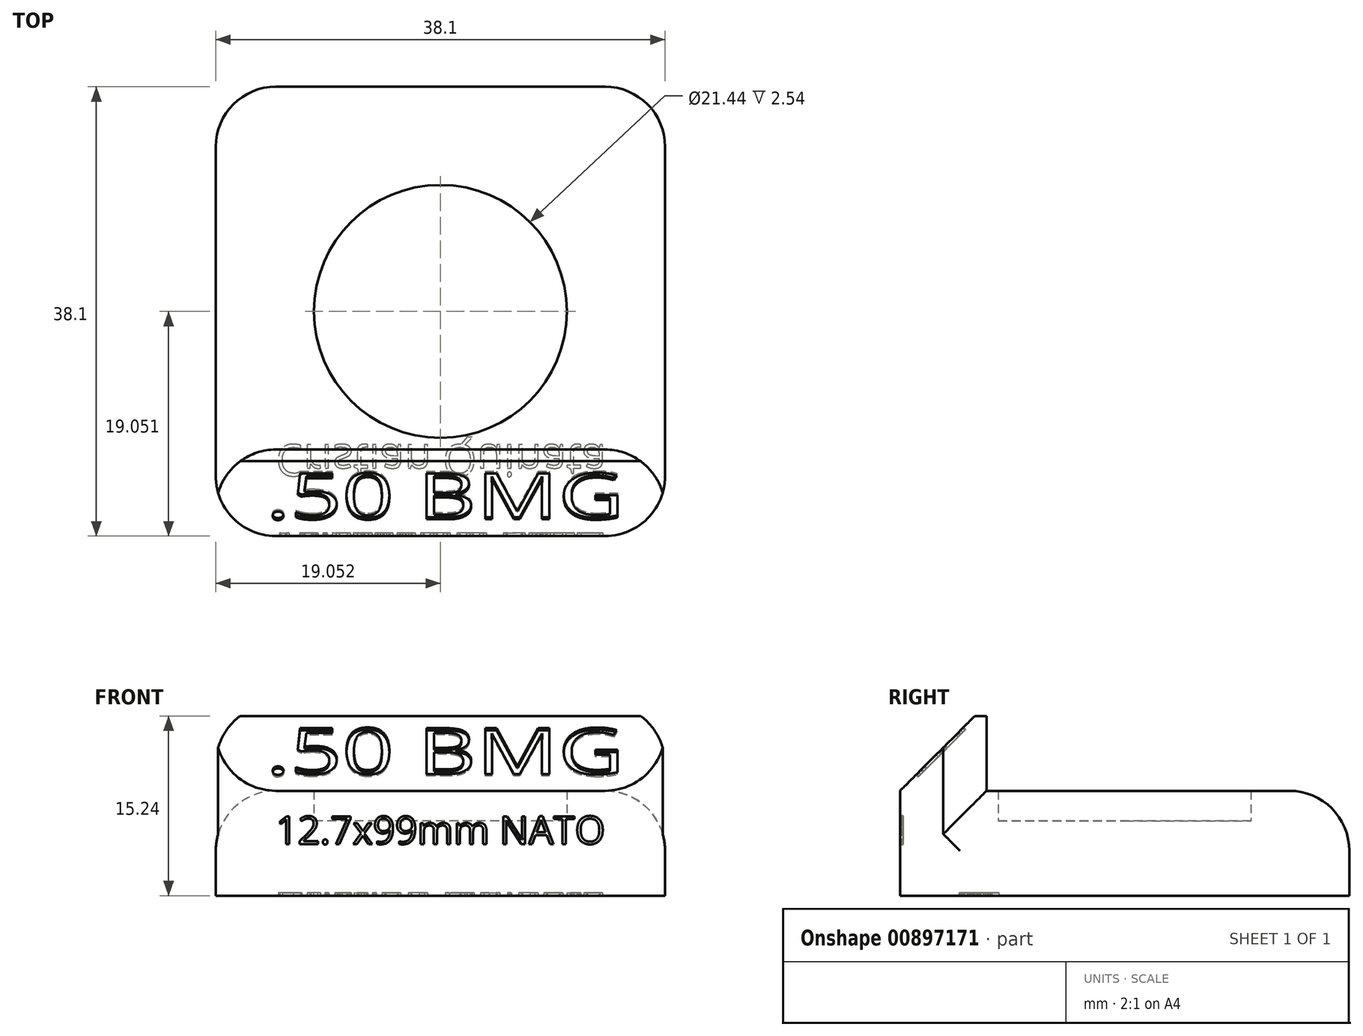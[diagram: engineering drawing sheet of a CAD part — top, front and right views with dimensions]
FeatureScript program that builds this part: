
annotation { "Feature Type Name" : "Feature", "Feature Type Description" : "" }
export const myFeature = defineFeature(function(context is Context, id is Id, definition is map)
    precondition{}
    {
        {
            var Q0;
            Q0=qCreatedBy(makeId("Top.planeOp"),FACE);
            var sketch = newSketch(context, id + "F0", { "sketchPlane" : qUnion([Q0])});
            skLineSegment(sketch, "E0.bottom", {"start": v(-52.13, -21.79) * mm, "end": v(-14.03, -21.79) * mm});
            skLineSegment(sketch, "E0.top", {"start": v(-52.13, -59.89) * mm, "end": v(-14.03, -59.89) * mm});
            skLineSegment(sketch, "E0.left", {"start": v(-52.13, -21.79) * mm, "end": v(-52.13, -59.89) * mm});
            skLineSegment(sketch, "E0.right", {"start": v(-14.03, -21.79) * mm, "end": v(-14.03, -59.89) * mm});
            skLineSegment(sketch, "E1", {"start": v(-33.08, -21.79) * mm, "end": v(-33.08, -59.89) * mm});
            skCircle(sketch, "E2", {"center": v(-33.08, -40.84) * mm, "radius": 10.72 * mm});
            skCircle(sketch, "E3", {"center": v(-33.08, -40.84) * mm, "radius": 10.21 * mm});
            skLineSegment(sketch, "E4", {"start": v(-52.13, -47.19) * mm, "end": v(-39.43, -59.89) * mm});
            skLineSegment(sketch, "E5", {"start": v(-14.03, -47.19) * mm, "end": v(-26.73, -59.89) * mm});
            skLineSegment(sketch, "E6", {"start": v(-52.13, -34.49) * mm, "end": v(-39.43, -21.79) * mm});
            skLineSegment(sketch, "E7", {"start": v(-26.73, -21.79) * mm, "end": v(-14.03, -34.49) * mm});
            skSolve(sketch);
        }
        {
            var Q0;
            {var subQ0=sQuery(id+"F0.wireOp",EDGE,"E2");var subQ1=sQuery(id+"F0.wireOp",EDGE,"E1");var subQ2=makeQuery(id+"F0.imprint","INTERSECT",VERTEX,{"disambiguationData":[OD(0.0)],"derivedFrom":[subQ1,subQ0]});Q0=makeQuery(id+"F0.imprint","IMPRINT",FACE,{"disambiguationData":[TD([[makeQuery(id+"F0.imprint","IMPRINT",EDGE,{"disambiguationData":[TD([[subQ2,-1.0]])],"derivedFrom":subQ1}),-1.0]])]});}
            var Q1;
            {var subQ3=sQuery(id+"F0.wireOp",EDGE,"E4");Q1=makeQuery(id+"F0.imprint","IMPRINT",FACE,{"disambiguationData":[TD([[makeQuery(id+"F0.imprint","IMPRINT",EDGE,{"derivedFrom":subQ3}),-1.0]])]});}
            var Q2;
            {var subQ0=sQuery(id+"F0.wireOp",EDGE,"E3");var subQ1=sQuery(id+"F0.wireOp",EDGE,"E1");var subQ2=makeQuery(id+"F0.imprint","INTERSECT",VERTEX,{"disambiguationData":[OD(0.0)],"derivedFrom":[subQ1,subQ0]});Q2=makeQuery(id+"F0.imprint","IMPRINT",FACE,{"disambiguationData":[TD([[makeQuery(id+"F0.imprint","IMPRINT",EDGE,{"disambiguationData":[TD([[subQ2,-1.0]])],"derivedFrom":subQ1}),-1.0]])]});}
            var Q3;
            {var subQ0=sQuery(id+"F0.wireOp",EDGE,"E3");var subQ1=sQuery(id+"F0.wireOp",EDGE,"E1");var subQ2=makeQuery(id+"F0.imprint","INTERSECT",VERTEX,{"disambiguationData":[OD(0.0)],"derivedFrom":[subQ1,subQ0]});Q3=makeQuery(id+"F0.imprint","IMPRINT",FACE,{"disambiguationData":[TD([[makeQuery(id+"F0.imprint","IMPRINT",EDGE,{"disambiguationData":[TD([[subQ2,-1.0]])],"derivedFrom":subQ1}),1.0]])]});}
            var Q4;
            {var subQ3=sQuery(id+"F0.wireOp",EDGE,"E7");Q4=makeQuery(id+"F0.imprint","IMPRINT",FACE,{"disambiguationData":[TD([[makeQuery(id+"F0.imprint","IMPRINT",EDGE,{"derivedFrom":subQ3}),1.0]])]});}
            var Q5;
            {var subQ3=sQuery(id+"F0.wireOp",EDGE,"E5");Q5=makeQuery(id+"F0.imprint","IMPRINT",FACE,{"disambiguationData":[TD([[makeQuery(id+"F0.imprint","IMPRINT",EDGE,{"derivedFrom":subQ3}),1.0]])]});}
            var Q6;
            {var subQ6=sQuery(id+"F0.wireOp",EDGE,"E4");Q6=makeQuery(id+"F0.imprint","IMPRINT",FACE,{"disambiguationData":[TD([[makeQuery(id+"F0.imprint","IMPRINT",EDGE,{"derivedFrom":subQ6}),1.0]])]});}
            var Q7;
            {var subQ7=sQuery(id+"F0.wireOp",EDGE,"E5");Q7=makeQuery(id+"F0.imprint","IMPRINT",FACE,{"disambiguationData":[TD([[makeQuery(id+"F0.imprint","IMPRINT",EDGE,{"derivedFrom":subQ7}),-1.0]])]});}
            var Q8;
            {var subQ3=sQuery(id+"F0.wireOp",EDGE,"E6");Q8=makeQuery(id+"F0.imprint","IMPRINT",FACE,{"disambiguationData":[TD([[makeQuery(id+"F0.imprint","IMPRINT",EDGE,{"derivedFrom":subQ3}),1.0]])]});}
            var Q9;
            {var subQ0=sQuery(id+"F0.wireOp",EDGE,"E2");var subQ1=sQuery(id+"F0.wireOp",EDGE,"E1");var subQ2=makeQuery(id+"F0.imprint","INTERSECT",VERTEX,{"disambiguationData":[OD(0.0)],"derivedFrom":[subQ1,subQ0]});Q9=makeQuery(id+"F0.imprint","IMPRINT",FACE,{"disambiguationData":[TD([[makeQuery(id+"F0.imprint","IMPRINT",EDGE,{"disambiguationData":[TD([[subQ2,-1.0]])],"derivedFrom":subQ1}),1.0]])]});}
            extrude(context, id + "F1", {"entities" : qUnion([Q0, Q1, Q2, Q3, Q4, Q5, Q6, Q7, Q8, Q9]), "depth" : 6.35 * mm, "offsetDistance" : 25.4 * mm});
        }
        {
            var Q0;
            {var subQ6=sQuery(id+"F0.wireOp",EDGE,"E4");Q0=makeQuery(id+"F0.imprint","IMPRINT",FACE,{"disambiguationData":[TD([[makeQuery(id+"F0.imprint","IMPRINT",EDGE,{"derivedFrom":subQ6}),1.0]])]});}
            var Q1;
            {var subQ7=sQuery(id+"F0.wireOp",EDGE,"E5");Q1=makeQuery(id+"F0.imprint","IMPRINT",FACE,{"disambiguationData":[TD([[makeQuery(id+"F0.imprint","IMPRINT",EDGE,{"derivedFrom":subQ7}),-1.0]])]});}
            var Q2;
            {var subQ3=sQuery(id+"F0.wireOp",EDGE,"E4");Q2=makeQuery(id+"F0.imprint","IMPRINT",FACE,{"disambiguationData":[TD([[makeQuery(id+"F0.imprint","IMPRINT",EDGE,{"derivedFrom":subQ3}),-1.0]])]});}
            var Q3;
            {var subQ3=sQuery(id+"F0.wireOp",EDGE,"E5");Q3=makeQuery(id+"F0.imprint","IMPRINT",FACE,{"disambiguationData":[TD([[makeQuery(id+"F0.imprint","IMPRINT",EDGE,{"derivedFrom":subQ3}),1.0]])]});}
            var Q4;
            {var subQ3=sQuery(id+"F0.wireOp",EDGE,"E7");Q4=makeQuery(id+"F0.imprint","IMPRINT",FACE,{"disambiguationData":[TD([[makeQuery(id+"F0.imprint","IMPRINT",EDGE,{"derivedFrom":subQ3}),1.0]])]});}
            var Q5;
            {var subQ3=sQuery(id+"F0.wireOp",EDGE,"E6");Q5=makeQuery(id+"F0.imprint","IMPRINT",FACE,{"disambiguationData":[TD([[makeQuery(id+"F0.imprint","IMPRINT",EDGE,{"derivedFrom":subQ3}),1.0]])]});}
            extrude(context, id + "F2", {"entities" : qUnion([Q0, Q1, Q2, Q3, Q4, Q5]), "operationType" : NewBodyOperationType.ADD, "depth" : 8.9 * mm, "offsetDistance" : 25.4 * mm});
        }
        {
            var Q0;
            Q0=makeQuery(id+"F2.opExtrude","CAP_FACE",FACE,{"disambiguationData":[OSD([sQuery(id+"F0.wireOp",EDGE,"E0.bottom"),sQuery(id+"F0.wireOp",EDGE,"E0.top"),sQuery(id+"F0.wireOp",EDGE,"E0.left"),sQuery(id+"F0.wireOp",EDGE,"E0.right"),sQuery(id+"F0.wireOp",EDGE,"E2")])],"isStart":false});
            var sketch = newSketch(context, id + "F3", { "sketchPlane" : qUnion([Q0])});
            skLineSegment(sketch, "E8", {"start": v(-52.13, -59.89) * mm, "end": v(-52.13, -52.56) * mm});
            skLineSegment(sketch, "E9", {"start": v(-52.13, -52.56) * mm, "end": v(-14.03, -52.56) * mm});
            skLineSegment(sketch, "E10", {"start": v(-14.03, -52.56) * mm, "end": v(-14.03, -59.89) * mm});
            skLineSegment(sketch, "E11", {"start": v(-14.03, -59.89) * mm, "end": v(-52.13, -59.89) * mm});
            skSolve(sketch);
        }
        {
            var Q0;
            Q0=makeQuery(id+"F3.imprint","IMPRINT",FACE,{"disambiguationData":[TD([[makeQuery(id+"F3.imprint","IMPRINT",EDGE,{"derivedFrom":sQuery(id+"F3.wireOp",EDGE,"E8")}),1.0]])]});
            extrude(context, id + "F4", {"entities" : qUnion([Q0]), "operationType" : NewBodyOperationType.ADD, "depth" : 6.35 * mm, "offsetDistance" : 25.4 * mm});
        }
        {
            var Q0;
            Q0=makeQuery(id+"F4.opExtrude","CAP_EDGE",EDGE,{"disambiguationData":[OSD([sQuery(id+"F3.wireOp",EDGE,"E11")])],"isStart":false});
            chamfer(context, id + "F5", {"entities" : qUnion([Q0]), "width" : 6.35 * mm, "tangentPropagation" : true});
        }
        {
            var Q0;
            {var subQ0=sQuery(id+"F0.wireOp",EDGE,"E0.left");var subQ1=sQuery(id+"F0.wireOp",EDGE,"E0.top");Q0=makeQuery(id+"F4.boolean.opBoolean","MERGE",EDGE,{"derivedFrom":[makeQuery(id+"FzP8uQMfJsJzeae_0.boolean.opBoolean","MERGE",EDGE,{"derivedFrom":[makeQuery(id+"F2.boolean.opBoolean","MERGE",EDGE,{"derivedFrom":[makeQuery(id+"F1.opExtrude","SWEPT_EDGE",EDGE,{"disambiguationData":[OSD([subQ1,subQ0])]}),makeQuery(id+"F2.opExtrude","SWEPT_EDGE",EDGE,{"disambiguationData":[OSD([subQ1,subQ0])]})]}),makeQuery(id+"FzP8uQMfJsJzeae_0.opExtrude","SWEPT_EDGE",EDGE,{"disambiguationData":[OSD([subQ1,subQ0])]})]}),makeQuery(id+"F4.opExtrude","SWEPT_EDGE",EDGE,{"disambiguationData":[OSD([sQuery(id+"F3.wireOp",EDGE,"E8"),sQuery(id+"F3.wireOp",EDGE,"E11")])]})]});}
            var Q1;
            {var subQ0=sQuery(id+"F0.wireOp",EDGE,"E0.right");var subQ1=sQuery(id+"F0.wireOp",EDGE,"E0.top");Q1=makeQuery(id+"F4.boolean.opBoolean","MERGE",EDGE,{"derivedFrom":[makeQuery(id+"FzP8uQMfJsJzeae_0.boolean.opBoolean","MERGE",EDGE,{"derivedFrom":[makeQuery(id+"F2.boolean.opBoolean","MERGE",EDGE,{"derivedFrom":[makeQuery(id+"F1.opExtrude","SWEPT_EDGE",EDGE,{"disambiguationData":[OSD([subQ1,subQ0])]}),makeQuery(id+"F2.opExtrude","SWEPT_EDGE",EDGE,{"disambiguationData":[OSD([subQ1,subQ0])]})]}),makeQuery(id+"FzP8uQMfJsJzeae_0.opExtrude","SWEPT_EDGE",EDGE,{"disambiguationData":[OSD([subQ1,subQ0])]})]}),makeQuery(id+"F4.opExtrude","SWEPT_EDGE",EDGE,{"disambiguationData":[OSD([sQuery(id+"F3.wireOp",EDGE,"E10"),sQuery(id+"F3.wireOp",EDGE,"E11")])]})]});}
            var Q2;
            {var subQ0=sQuery(id+"F0.wireOp",EDGE,"E0.right");var subQ1=sQuery(id+"F0.wireOp",EDGE,"E0.bottom");Q2=makeQuery(id+"FzP8uQMfJsJzeae_0.boolean.opBoolean","MERGE",EDGE,{"derivedFrom":[makeQuery(id+"F2.boolean.opBoolean","MERGE",EDGE,{"derivedFrom":[makeQuery(id+"F1.opExtrude","SWEPT_EDGE",EDGE,{"disambiguationData":[OSD([subQ1,subQ0])]}),makeQuery(id+"F2.opExtrude","SWEPT_EDGE",EDGE,{"disambiguationData":[OSD([subQ1,subQ0])]})]}),makeQuery(id+"FzP8uQMfJsJzeae_0.opExtrude","SWEPT_EDGE",EDGE,{"disambiguationData":[OSD([subQ1,subQ0])]})]});}
            var Q3;
            {var subQ0=sQuery(id+"F0.wireOp",EDGE,"E0.left");var subQ1=sQuery(id+"F0.wireOp",EDGE,"E0.bottom");Q3=makeQuery(id+"FzP8uQMfJsJzeae_0.boolean.opBoolean","MERGE",EDGE,{"derivedFrom":[makeQuery(id+"F2.boolean.opBoolean","MERGE",EDGE,{"derivedFrom":[makeQuery(id+"F1.opExtrude","SWEPT_EDGE",EDGE,{"disambiguationData":[OSD([subQ1,subQ0])]}),makeQuery(id+"F2.opExtrude","SWEPT_EDGE",EDGE,{"disambiguationData":[OSD([subQ1,subQ0])]})]}),makeQuery(id+"FzP8uQMfJsJzeae_0.opExtrude","SWEPT_EDGE",EDGE,{"disambiguationData":[OSD([subQ1,subQ0])]})]});}
            var Q4;
            Q4=makeQuery(id+"F2.opExtrude","CAP_EDGE",EDGE,{"disambiguationData":[OSD([sQuery(id+"F0.wireOp",EDGE,"E0.right")])],"isStart":false});
            var Q5;
            Q5=makeQuery(id+"F2.opExtrude","CAP_EDGE",EDGE,{"disambiguationData":[OSD([sQuery(id+"F0.wireOp",EDGE,"E0.bottom")])],"isStart":false});
            var Q6;
            Q6=makeQuery(id+"F2.opExtrude","CAP_EDGE",EDGE,{"disambiguationData":[OSD([sQuery(id+"F0.wireOp",EDGE,"E0.left")])],"isStart":false});
            var Q7;
            Q7=makeQuery(id+"F4.opExtrude","SWEPT_EDGE",EDGE,{"disambiguationData":[OSD([sQuery(id+"F0.wireOp",EDGE,"E0.left"),sQuery(id+"F3.wireOp",EDGE,"E8"),sQuery(id+"F3.wireOp",EDGE,"E9")])]});
            var Q8;
            Q8=makeQuery(id+"F4.opExtrude","SWEPT_EDGE",EDGE,{"disambiguationData":[OSD([sQuery(id+"F0.wireOp",EDGE,"E0.right"),sQuery(id+"F3.wireOp",EDGE,"E9"),sQuery(id+"F3.wireOp",EDGE,"E10")])]});
            fillet(context, id + "F6", {"entities" : qUnion([Q0, Q1, Q2, Q3, Q4, Q5, Q6, Q7, Q8]), "radius" : 5.08 * mm, "tangentPropagation" : true, "allowEdgeOverflow" : false});
        }
        {
            var Q0;
            Q0=makeQuery(id+"F5.opChamfer","BLEND_FACE",FACE,{"disambiguationData":[OSD([sQuery(id+"F3.wireOp",EDGE,"E11")])]});
            var sketch = newSketch(context, id + "F7", { "sketchPlane" : qUnion([Q0])});
            skText(sketch, "E12", { "text": ".50 BMG\n", "fontName": "OpenSans-Regular.ttf"});
            const initialGuessF7  = {"E12": [-0.04787, -0.03404, 1, 0, 0.00554]};
            skSetInitialGuess(sketch, initialGuessF7);
            skSolve(sketch);
        }
        {
            var Q0;
            Q0 = qSketchRegion(id + "F7", true);
            extrude(context, id + "F8", {"entities" : qUnion([Q0]), "operationType" : NewBodyOperationType.REMOVE, "oppositeDirection" : true, "depth" : 0.25 * mm, "offsetDistance" : 25.4 * mm});
        }
        {
            var Q0;
            {var subQ0=sQuery(id+"F0.wireOp",EDGE,"E0.top");Q0=makeQuery(id+"F4.boolean.opBoolean","MERGE",FACE,{"derivedFrom":[makeQuery(id+"F2.boolean.opBoolean","MERGE",FACE,{"derivedFrom":[makeQuery(id+"F1.opExtrude","SWEPT_FACE",FACE,{"disambiguationData":[OSD([subQ0])]}),makeQuery(id+"F2.opExtrude","SWEPT_FACE",FACE,{"disambiguationData":[OSD([subQ0])]})]}),makeQuery(id+"F4.opExtrude","SWEPT_FACE",FACE,{"disambiguationData":[OSD([sQuery(id+"F3.wireOp",EDGE,"E11")])]})]});}
            var sketch = newSketch(context, id + "F9", { "sketchPlane" : qUnion([Q0])});
            skText(sketch, "E13", { "text": "12.7x99mm NATO\n", "fontName": "OpenSans-Regular.ttf"});
            const initialGuessF9  = {"E13": [-0.04705, 0.00438, 1, 0, 0.00237]};
            skSetInitialGuess(sketch, initialGuessF9);
            skSolve(sketch);
        }
        {
            var Q0;
            Q0 = qSketchRegion(id + "F9", true);
            extrude(context, id + "F10", {"entities" : qUnion([Q0]), "operationType" : NewBodyOperationType.REMOVE, "oppositeDirection" : true, "depth" : 0.25 * mm, "offsetDistance" : 25.4 * mm});
        }
        {
            var Q0;
            Q0=makeQuery(id+"F1.opExtrude","CAP_FACE",FACE,{"disambiguationData":[OSD([sQuery(id+"F0.wireOp",EDGE,"E0.bottom"),sQuery(id+"F0.wireOp",EDGE,"E0.top"),sQuery(id+"F0.wireOp",EDGE,"E0.left"),sQuery(id+"F0.wireOp",EDGE,"E0.right")])],"isStart":true});
            var sketch = newSketch(context, id + "F11", { "sketchPlane" : qUnion([Q0])});
            skText(sketch, "E14", { "text": "Cristian Quinata ", "fontName": "OpenSans-Regular.ttf"});
            const initialGuessF11  = {"E14": [-0.04705, 0.05213, 1, 0, 0.00268]};
            skSetInitialGuess(sketch, initialGuessF11);
            skSolve(sketch);
        }
        {
            var Q0;
            Q0 = qSketchRegion(id + "F11", true);
            extrude(context, id + "F12", {"entities" : qUnion([Q0]), "operationType" : NewBodyOperationType.REMOVE, "oppositeDirection" : true, "depth" : 0.25 * mm, "offsetDistance" : 25.4 * mm});
        }
    });
